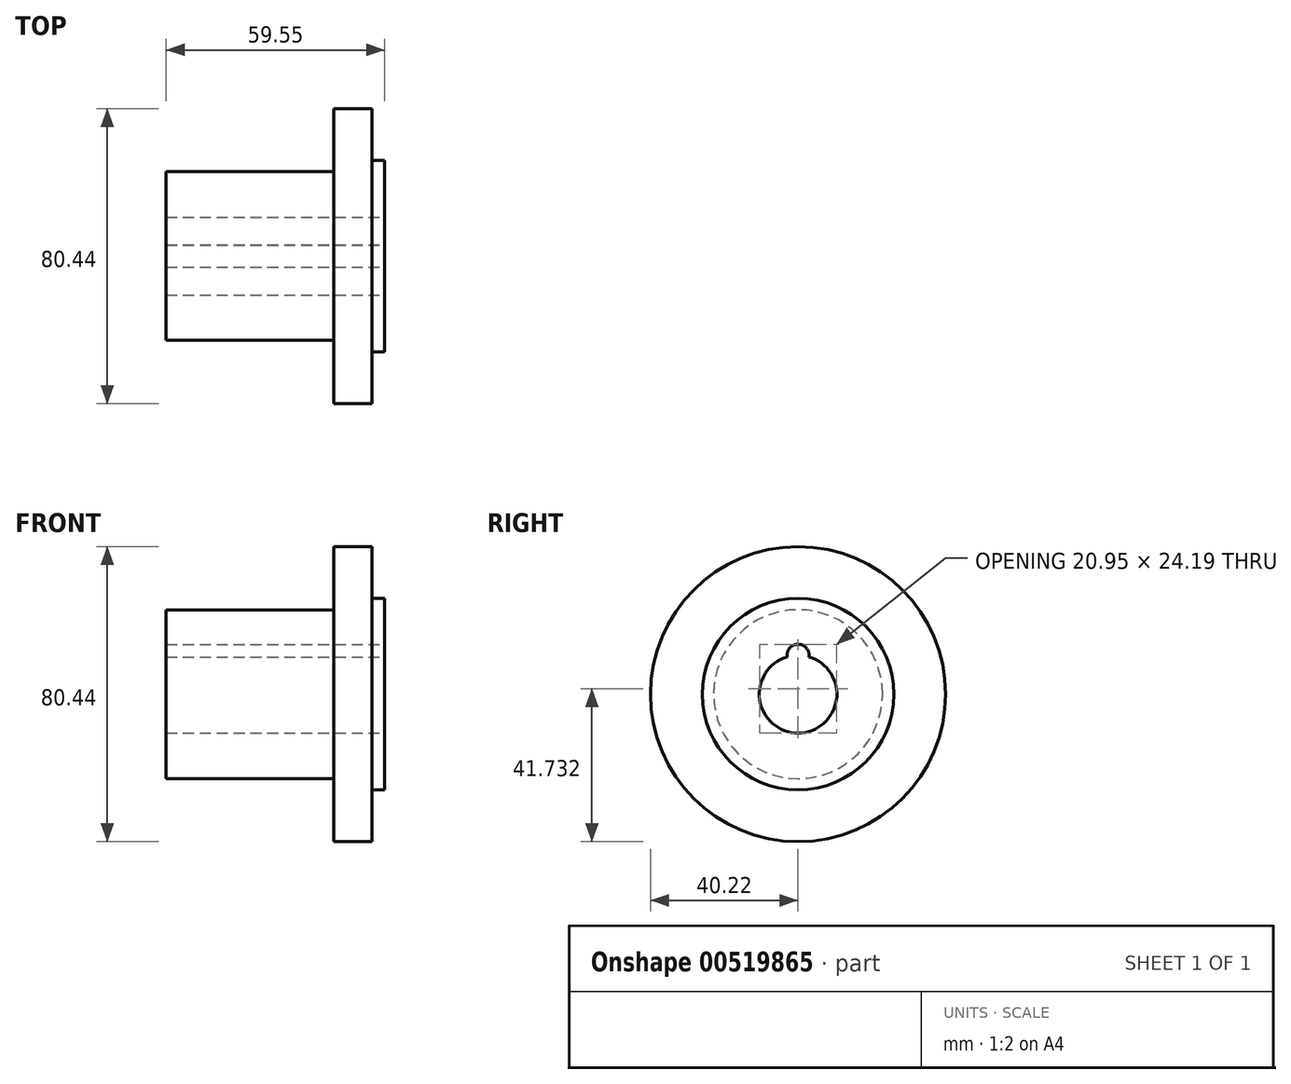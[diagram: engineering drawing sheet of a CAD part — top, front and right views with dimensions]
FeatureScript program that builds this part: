
annotation { "Feature Type Name" : "Feature", "Feature Type Description" : "" }
export const myFeature = defineFeature(function(context is Context, id is Id, definition is map)
    precondition{}
    {
        {
            var Q0;
            Q0=qCreatedBy(makeId("Front.planeOp"),FACE);
            var sketch = newSketch(context, id + "F0", { "sketchPlane" : qUnion([Q0])});
            skLineSegment(sketch, "E0", {"start": v(0, 10.58) * mm, "end": v(-59.55, 10.58) * mm});
            skLineSegment(sketch, "E1", {"start": v(-59.55, 10.58) * mm, "end": v(-59.55, 23) * mm});
            skLineSegment(sketch, "E2", {"start": v(-59.55, 23) * mm, "end": v(-13.83, 23) * mm});
            skLineSegment(sketch, "E3", {"start": v(-13.83, 23) * mm, "end": v(-13.83, 40.22) * mm});
            skLineSegment(sketch, "E4", {"start": v(-13.83, 40.22) * mm, "end": v(-3.39, 40.22) * mm});
            skLineSegment(sketch, "E5", {"start": v(-3.39, 40.22) * mm, "end": v(-3.39, 26.1) * mm});
            skLineSegment(sketch, "E6", {"start": v(-3.39, 26.1) * mm, "end": v(0, 26.1) * mm});
            skLineSegment(sketch, "E7", {"start": v(0, 26.1) * mm, "end": v(0, 10.58) * mm});
            skLineSegment(sketch, "E8", {"start": v(0, 0) * mm, "end": v(-136.44, 0) * mm, "construction": true});
            skSolve(sketch);
        }
        {
            var Q0;
            Q0 = qSketchRegion(id + "F0", true);
            var Q1;
            Q1=sQuery(id+"F0.wireOp",EDGE,"E8");
            revolve(context, id + "F1", {"entities" : qUnion([Q0]), "axis" : qUnion([Q1]), "revolveType" : RevolveType.FULL});
        }
        {
            var Q0;
            Q0=makeQuery(id+"F1.opRevolve","SWEPT_FACE",FACE,{"disambiguationData":[OSD([sQuery(id+"F0.wireOp",EDGE,"E7")])]});
            var sketch = newSketch(context, id + "F2", { "sketchPlane" : qUnion([Q0])});
            skCircle(sketch, "E9", {"center": v(0, 10.58) * mm, "radius": 3.02 * mm});
            skSolve(sketch);
        }
        {
            var Q0;
            Q0 = qSketchRegion(id + "F2", true);
            extrude(context, id + "F3", {"entities" : qUnion([Q0]), "operationType" : NewBodyOperationType.REMOVE, "endBound" : BoundingType.THROUGH_ALL, "oppositeDirection" : true, "depth" : 25.4 * mm, "offsetDistance" : 25.4 * mm});
        }
    });
